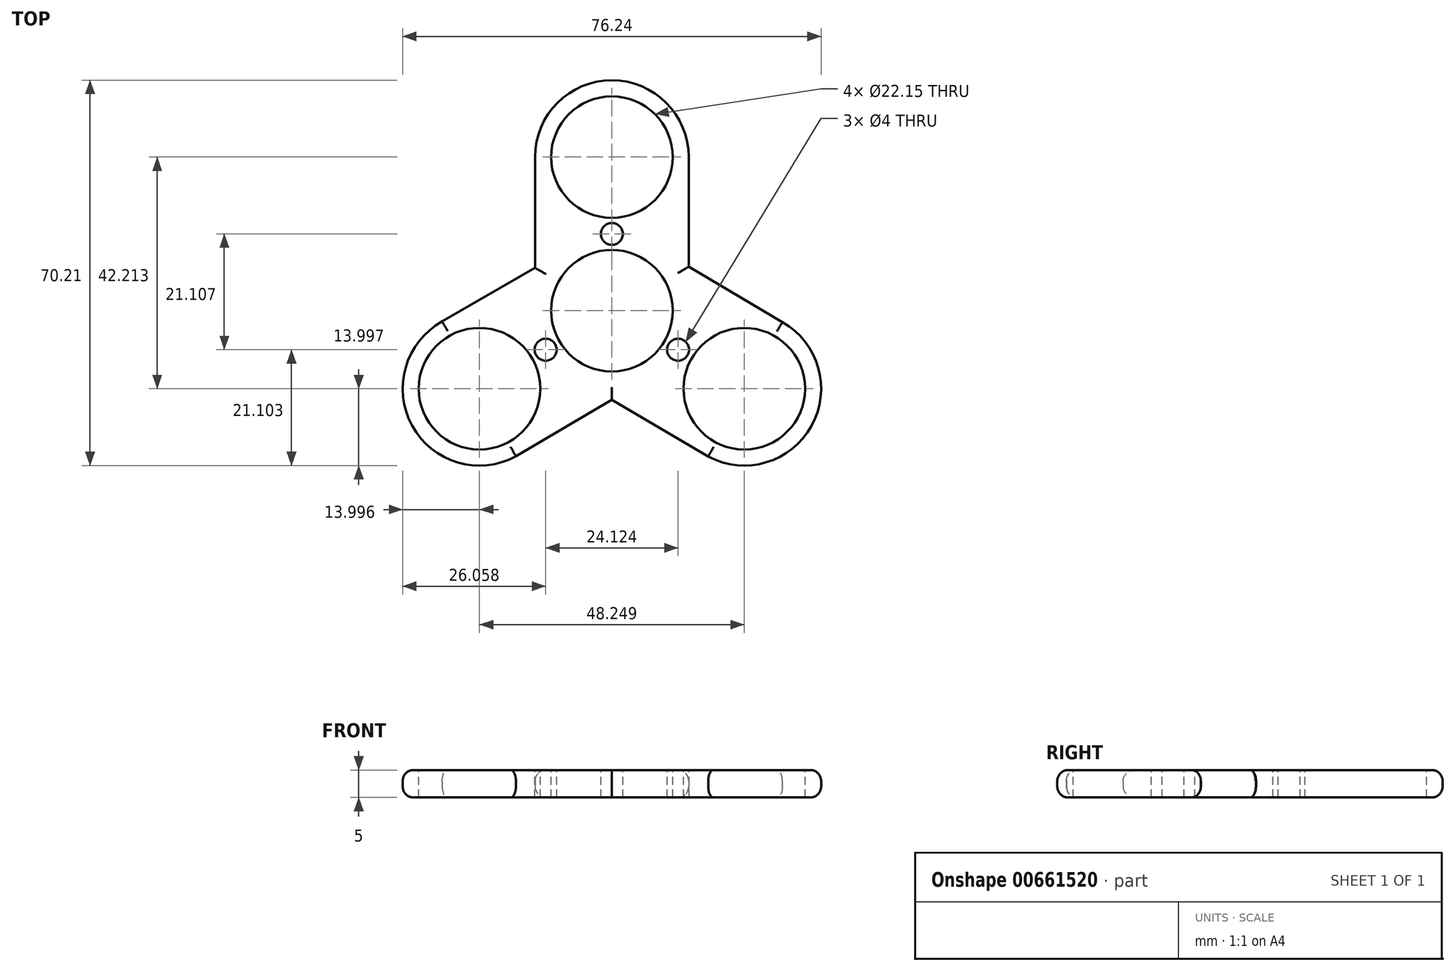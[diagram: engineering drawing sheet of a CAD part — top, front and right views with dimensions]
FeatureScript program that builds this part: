
annotation { "Feature Type Name" : "Feature", "Feature Type Description" : "" }
export const myFeature = defineFeature(function(context is Context, id is Id, definition is map)
    precondition{}
    {
        {
            var Q0;
            Q0=qCreatedBy(makeId("Top.planeOp"),FACE);
            var sketch = newSketch(context, id + "F0", { "sketchPlane" : qUnion([Q0])});
            skCircle(sketch, "E0", {"center": v(0, 0) * mm, "radius": 14 * mm});
            skCircle(sketch, "E1", {"center": v(0, 28) * mm, "radius": 14 * mm});
            skCircle(sketch, "E2", {"center": v(-24.12, -14.21) * mm, "radius": 14 * mm});
            skCircle(sketch, "E3", {"center": v(24.12, -14.21) * mm, "radius": 14 * mm});
            skLineSegment(sketch, "E4", {"start": v(-14, 28) * mm, "end": v(-14, 0) * mm});
            skLineSegment(sketch, "E5", {"start": v(14, 28) * mm, "end": v(14, 0) * mm});
            skLineSegment(sketch, "E6", {"start": v(-31.34, -2.22) * mm, "end": v(-4.7, 13.19) * mm});
            skLineSegment(sketch, "E7", {"start": v(31.06, -2.05) * mm, "end": v(7.1, 12.06) * mm});
            skLineSegment(sketch, "E8", {"start": v(-17.49, -26.54) * mm, "end": v(7.1, -12.06) * mm});
            skLineSegment(sketch, "E9", {"start": v(17.55, -26.57) * mm, "end": v(-7.1, -12.07) * mm});
            skSolve(sketch);
        }
        {
            var Q0;
            {var subQ0=sQuery(id+"F0.wireOp",EDGE,"E6");var subQ1=sQuery(id+"F0.wireOp",EDGE,"E2");var subQ3=makeQuery(id+"F0.imprint","INTERSECT",VERTEX,{"disambiguationData":[OD(1.0)],"derivedFrom":[subQ1,subQ0]});Q0=makeQuery(id+"F0.imprint","IMPRINT",FACE,{"disambiguationData":[TD([[makeQuery(id+"F0.imprint","IMPRINT",EDGE,{"disambiguationData":[TD([[subQ3,1.0]])],"derivedFrom":subQ1}),1.0]])]});}
            var Q1;
            {var subQ0=sQuery(id+"F0.wireOp",EDGE,"E0");var subQ7=makeQuery(id+"F0.imprint","INTERSECT",VERTEX,{"derivedFrom":[subQ0,sQuery(id+"F0.wireOp",EDGE,"E5")]});Q1=makeQuery(id+"F0.imprint","IMPRINT",FACE,{"disambiguationData":[TD([[makeQuery(id+"F0.imprint","IMPRINT",EDGE,{"disambiguationData":[TD([[subQ7,-1.0]])],"derivedFrom":subQ0}),1.0]])]});}
            var Q2;
            {var subQ3=sQuery(id+"F0.wireOp",EDGE,"E0");var subQ5=sQuery(id+"F0.wireOp",EDGE,"E6");var subQ7=makeQuery(id+"F0.imprint","INTERSECT",VERTEX,{"disambiguationData":[OD(0.0)],"derivedFrom":[subQ3,subQ5]});Q2=makeQuery(id+"F0.imprint","IMPRINT",FACE,{"disambiguationData":[TD([[makeQuery(id+"F0.imprint","IMPRINT",EDGE,{"disambiguationData":[TD([[subQ7,1.0]])],"derivedFrom":subQ3}),-1.0]])]});}
            var Q3;
            {var subQ0=sQuery(id+"F0.wireOp",EDGE,"E3");var subQ1=makeQuery(id+"F0.imprint","INTERSECT",VERTEX,{"derivedFrom":[subQ0,sQuery(id+"F0.wireOp",EDGE,"E7")]});Q3=makeQuery(id+"F0.imprint","IMPRINT",FACE,{"disambiguationData":[TD([[makeQuery(id+"F0.imprint","IMPRINT",EDGE,{"disambiguationData":[TD([[subQ1,-1.0]])],"derivedFrom":subQ0}),1.0]])]});}
            var Q4;
            {var subQ0=sQuery(id+"F0.wireOp",EDGE,"E1");var subQ1=makeQuery(id+"F0.imprint","INTERSECT",VERTEX,{"derivedFrom":[subQ0,sQuery(id+"F0.wireOp",EDGE,"E4")]});Q4=makeQuery(id+"F0.imprint","IMPRINT",FACE,{"disambiguationData":[TD([[makeQuery(id+"F0.imprint","IMPRINT",EDGE,{"disambiguationData":[TD([[subQ1,1.0]])],"derivedFrom":subQ0}),1.0]])]});}
            var Q5;
            {var subQ0=sQuery(id+"F0.wireOp",EDGE,"E5");var subQ1=sQuery(id+"F0.wireOp",EDGE,"E0");var subQ2=makeQuery(id+"F0.imprint","INTERSECT",VERTEX,{"derivedFrom":[subQ1,subQ0]});Q5=makeQuery(id+"F0.imprint","IMPRINT",FACE,{"disambiguationData":[TD([[makeQuery(id+"F0.imprint","IMPRINT",EDGE,{"disambiguationData":[TD([[subQ2,-1.0]])],"derivedFrom":subQ1}),-1.0]])]});}
            var Q6;
            {var subQ0=sQuery(id+"F0.wireOp",EDGE,"E7");var subQ1=sQuery(id+"F0.wireOp",EDGE,"E0");var subQ2=makeQuery(id+"F0.imprint","INTERSECT",VERTEX,{"derivedFrom":[subQ1,subQ0]});Q6=makeQuery(id+"F0.imprint","IMPRINT",FACE,{"disambiguationData":[TD([[makeQuery(id+"F0.imprint","IMPRINT",EDGE,{"disambiguationData":[TD([[subQ2,-1.0]])],"derivedFrom":subQ1}),-1.0]])]});}
            var Q7;
            {var subQ0=sQuery(id+"F0.wireOp",EDGE,"E4");var subQ1=sQuery(id+"F0.wireOp",EDGE,"E0");var subQ2=makeQuery(id+"F0.imprint","INTERSECT",VERTEX,{"derivedFrom":[subQ1,subQ0]});Q7=makeQuery(id+"F0.imprint","IMPRINT",FACE,{"disambiguationData":[TD([[makeQuery(id+"F0.imprint","IMPRINT",EDGE,{"disambiguationData":[TD([[subQ2,1.0]])],"derivedFrom":subQ1}),-1.0]])]});}
            var Q8;
            {var subQ0=sQuery(id+"F0.wireOp",EDGE,"E4");var subQ1=sQuery(id+"F0.wireOp",EDGE,"E0");var subQ2=makeQuery(id+"F0.imprint","INTERSECT",VERTEX,{"derivedFrom":[subQ1,subQ0]});Q8=makeQuery(id+"F0.imprint","IMPRINT",FACE,{"disambiguationData":[TD([[makeQuery(id+"F0.imprint","IMPRINT",EDGE,{"disambiguationData":[TD([[subQ2,-1.0]])],"derivedFrom":subQ1}),-1.0]])]});}
            var Q9;
            {var subQ0=sQuery(id+"F0.wireOp",EDGE,"E9");var subQ1=sQuery(id+"F0.wireOp",EDGE,"E0");var subQ2=makeQuery(id+"F0.imprint","INTERSECT",VERTEX,{"derivedFrom":[subQ1,subQ0]});Q9=makeQuery(id+"F0.imprint","IMPRINT",FACE,{"disambiguationData":[TD([[makeQuery(id+"F0.imprint","IMPRINT",EDGE,{"disambiguationData":[TD([[subQ2,1.0]])],"derivedFrom":subQ1}),-1.0]])]});}
            var Q10;
            {var subQ0=sQuery(id+"F0.wireOp",EDGE,"E8");var subQ1=sQuery(id+"F0.wireOp",EDGE,"E0");var subQ2=makeQuery(id+"F0.imprint","INTERSECT",VERTEX,{"derivedFrom":[subQ1,subQ0]});Q10=makeQuery(id+"F0.imprint","IMPRINT",FACE,{"disambiguationData":[TD([[makeQuery(id+"F0.imprint","IMPRINT",EDGE,{"disambiguationData":[TD([[subQ2,1.0]])],"derivedFrom":subQ1}),-1.0]])]});}
            var Q11;
            {var subQ0=sQuery(id+"F0.wireOp",EDGE,"E8");var subQ1=sQuery(id+"F0.wireOp",EDGE,"E0");var subQ2=makeQuery(id+"F0.imprint","INTERSECT",VERTEX,{"derivedFrom":[subQ1,subQ0]});Q11=makeQuery(id+"F0.imprint","IMPRINT",FACE,{"disambiguationData":[TD([[makeQuery(id+"F0.imprint","IMPRINT",EDGE,{"disambiguationData":[TD([[subQ2,-1.0]])],"derivedFrom":subQ1}),-1.0]])]});}
            var Q12;
            {var subQ0=sQuery(id+"F0.wireOp",EDGE,"E5");var subQ1=sQuery(id+"F0.wireOp",EDGE,"E0");var subQ2=makeQuery(id+"F0.imprint","INTERSECT",VERTEX,{"derivedFrom":[subQ1,subQ0]});Q12=makeQuery(id+"F0.imprint","IMPRINT",FACE,{"disambiguationData":[TD([[makeQuery(id+"F0.imprint","IMPRINT",EDGE,{"disambiguationData":[TD([[subQ2,1.0]])],"derivedFrom":subQ1}),-1.0]])]});}
            var Q13;
            {var subQ0=sQuery(id+"F0.wireOp",EDGE,"E6");var subQ1=sQuery(id+"F0.wireOp",EDGE,"E2");var subQ2=makeQuery(id+"F0.imprint","INTERSECT",VERTEX,{"disambiguationData":[OD(0.0)],"derivedFrom":[subQ1,subQ0]});Q13=makeQuery(id+"F0.imprint","IMPRINT",FACE,{"disambiguationData":[TD([[makeQuery(id+"F0.imprint","IMPRINT",EDGE,{"disambiguationData":[TD([[subQ2,1.0]])],"derivedFrom":subQ1}),1.0]])]});}
            var Q14;
            {var subQ0=sQuery(id+"F0.wireOp",EDGE,"E8");var subQ1=sQuery(id+"F0.wireOp",EDGE,"E2");var subQ2=makeQuery(id+"F0.imprint","INTERSECT",VERTEX,{"disambiguationData":[OD(0.0)],"derivedFrom":[subQ1,subQ0]});Q14=makeQuery(id+"F0.imprint","IMPRINT",FACE,{"disambiguationData":[TD([[makeQuery(id+"F0.imprint","IMPRINT",EDGE,{"disambiguationData":[TD([[subQ2,-1.0]])],"derivedFrom":subQ1}),1.0]])]});}
            var Q15;
            {var subQ0=sQuery(id+"F0.wireOp",EDGE,"E9");var subQ1=sQuery(id+"F0.wireOp",EDGE,"E3");var subQ2=makeQuery(id+"F0.imprint","INTERSECT",VERTEX,{"disambiguationData":[OD(0.0)],"derivedFrom":[subQ1,subQ0]});Q15=makeQuery(id+"F0.imprint","IMPRINT",FACE,{"disambiguationData":[TD([[makeQuery(id+"F0.imprint","IMPRINT",EDGE,{"disambiguationData":[TD([[subQ2,1.0]])],"derivedFrom":subQ1}),1.0]])]});}
            var Q16;
            {var subQ0=sQuery(id+"F0.wireOp",EDGE,"E6");var subQ1=sQuery(id+"F0.wireOp",EDGE,"E0");var subQ2=makeQuery(id+"F0.imprint","INTERSECT",VERTEX,{"disambiguationData":[OD(0.0)],"derivedFrom":[subQ1,subQ0]});Q16=makeQuery(id+"F0.imprint","IMPRINT",FACE,{"disambiguationData":[TD([[makeQuery(id+"F0.imprint","IMPRINT",EDGE,{"disambiguationData":[TD([[subQ2,-1.0]])],"derivedFrom":subQ1}),1.0]])]});}
            extrude(context, id + "F1", {"entities" : qUnion([Q0, Q1, Q2, Q3, Q4, Q5, Q6, Q7, Q8, Q9, Q10, Q11, Q12, Q13, Q14, Q15, Q16]), "depth" : 5 * mm, "offsetDistance" : 25 * mm});
        }
        {
            var Q0;
            Q0=makeQuery(id+"F1.opExtrude","CAP_FACE",FACE,{"disambiguationData":[OSD([sQuery(id+"F0.wireOp",EDGE,"E1"),sQuery(id+"F0.wireOp",EDGE,"E2"),sQuery(id+"F0.wireOp",EDGE,"E3"),sQuery(id+"F0.wireOp",EDGE,"E4"),sQuery(id+"F0.wireOp",EDGE,"E5"),sQuery(id+"F0.wireOp",EDGE,"E6"),sQuery(id+"F0.wireOp",EDGE,"E7"),sQuery(id+"F0.wireOp",EDGE,"E8"),sQuery(id+"F0.wireOp",EDGE,"E9")])],"isStart":false});
            var sketch = newSketch(context, id + "F2", { "sketchPlane" : qUnion([Q0])});
            skCircle(sketch, "E10", {"center": v(0, 0) * mm, "radius": 11.07 * mm});
            skCircle(sketch, "E11", {"center": v(0, 28) * mm, "radius": 11.07 * mm});
            skCircle(sketch, "E12", {"center": v(24.12, -14.21) * mm, "radius": 11.07 * mm});
            skCircle(sketch, "E13", {"center": v(-24.12, -14.21) * mm, "radius": 11.07 * mm});
            skCircle(sketch, "E14", {"center": v(0, 14) * mm, "radius": 2 * mm});
            skCircle(sketch, "E15", {"center": v(-12.06, -7.1) * mm, "radius": 2 * mm});
            skCircle(sketch, "E16", {"center": v(12.06, -7.1) * mm, "radius": 2 * mm});
            skSolve(sketch);
        }
        {
            var Q0;
            Q0 = qSketchRegion(id + "F2", true);
            extrude(context, id + "F3", {"entities" : qUnion([Q0]), "operationType" : NewBodyOperationType.REMOVE, "endBound" : BoundingType.THROUGH_ALL, "oppositeDirection" : true, "depth" : 25 * mm, "offsetDistance" : 25 * mm});
        }
        {
            var Q0;
            Q0=makeQuery(id+"F1.opExtrude","CAP_EDGE",EDGE,{"disambiguationData":[OSD([sQuery(id+"F0.wireOp",EDGE,"E6")])],"isStart":false});
            var Q1;
            Q1=makeQuery(id+"F1.opExtrude","CAP_EDGE",EDGE,{"disambiguationData":[OSD([sQuery(id+"F0.wireOp",EDGE,"E2")])],"isStart":false});
            var Q2;
            Q2=makeQuery(id+"F1.opExtrude","CAP_EDGE",EDGE,{"disambiguationData":[OSD([sQuery(id+"F0.wireOp",EDGE,"E8")])],"isStart":false});
            var Q3;
            Q3=makeQuery(id+"F1.opExtrude","CAP_EDGE",EDGE,{"disambiguationData":[OSD([sQuery(id+"F0.wireOp",EDGE,"E9")])],"isStart":false});
            var Q4;
            Q4=makeQuery(id+"F1.opExtrude","CAP_EDGE",EDGE,{"disambiguationData":[OSD([sQuery(id+"F0.wireOp",EDGE,"E3")])],"isStart":false});
            var Q5;
            Q5=makeQuery(id+"F1.opExtrude","CAP_EDGE",EDGE,{"disambiguationData":[OSD([sQuery(id+"F0.wireOp",EDGE,"E7")])],"isStart":false});
            var Q6;
            Q6=makeQuery(id+"F1.opExtrude","CAP_EDGE",EDGE,{"disambiguationData":[OSD([sQuery(id+"F0.wireOp",EDGE,"E5")])],"isStart":false});
            var Q7;
            Q7=makeQuery(id+"F1.opExtrude","CAP_EDGE",EDGE,{"disambiguationData":[OSD([sQuery(id+"F0.wireOp",EDGE,"E1")])],"isStart":false});
            var Q8;
            Q8=makeQuery(id+"F1.opExtrude","CAP_EDGE",EDGE,{"disambiguationData":[OSD([sQuery(id+"F0.wireOp",EDGE,"E4")])],"isStart":false});
            var Q9;
            Q9=makeQuery(id+"F1.opExtrude","CAP_EDGE",EDGE,{"disambiguationData":[OSD([sQuery(id+"F0.wireOp",EDGE,"E8")])],"isStart":true});
            var Q10;
            Q10=makeQuery(id+"F1.opExtrude","CAP_EDGE",EDGE,{"disambiguationData":[OSD([sQuery(id+"F0.wireOp",EDGE,"E2")])],"isStart":true});
            var Q11;
            Q11=makeQuery(id+"F1.opExtrude","CAP_EDGE",EDGE,{"disambiguationData":[OSD([sQuery(id+"F0.wireOp",EDGE,"E6")])],"isStart":true});
            var Q12;
            Q12=makeQuery(id+"F1.opExtrude","CAP_EDGE",EDGE,{"disambiguationData":[OSD([sQuery(id+"F0.wireOp",EDGE,"E4")])],"isStart":true});
            var Q13;
            Q13=makeQuery(id+"F1.opExtrude","CAP_EDGE",EDGE,{"disambiguationData":[OSD([sQuery(id+"F0.wireOp",EDGE,"E1")])],"isStart":true});
            var Q14;
            Q14=makeQuery(id+"F1.opExtrude","CAP_EDGE",EDGE,{"disambiguationData":[OSD([sQuery(id+"F0.wireOp",EDGE,"E5")])],"isStart":true});
            var Q15;
            Q15=makeQuery(id+"F1.opExtrude","CAP_EDGE",EDGE,{"disambiguationData":[OSD([sQuery(id+"F0.wireOp",EDGE,"E7")])],"isStart":true});
            var Q16;
            Q16=makeQuery(id+"F1.opExtrude","CAP_EDGE",EDGE,{"disambiguationData":[OSD([sQuery(id+"F0.wireOp",EDGE,"E3")])],"isStart":true});
            var Q17;
            Q17=makeQuery(id+"F1.opExtrude","CAP_EDGE",EDGE,{"disambiguationData":[OSD([sQuery(id+"F0.wireOp",EDGE,"E9")])],"isStart":true});
            fillet(context, id + "F4", {"entities" : qUnion([Q0, Q1, Q2, Q3, Q4, Q5, Q6, Q7, Q8, Q9, Q10, Q11, Q12, Q13, Q14, Q15, Q16, Q17]), "radius" : 2 * mm, "tangentPropagation" : true, "allowEdgeOverflow" : false});
        }
    });
